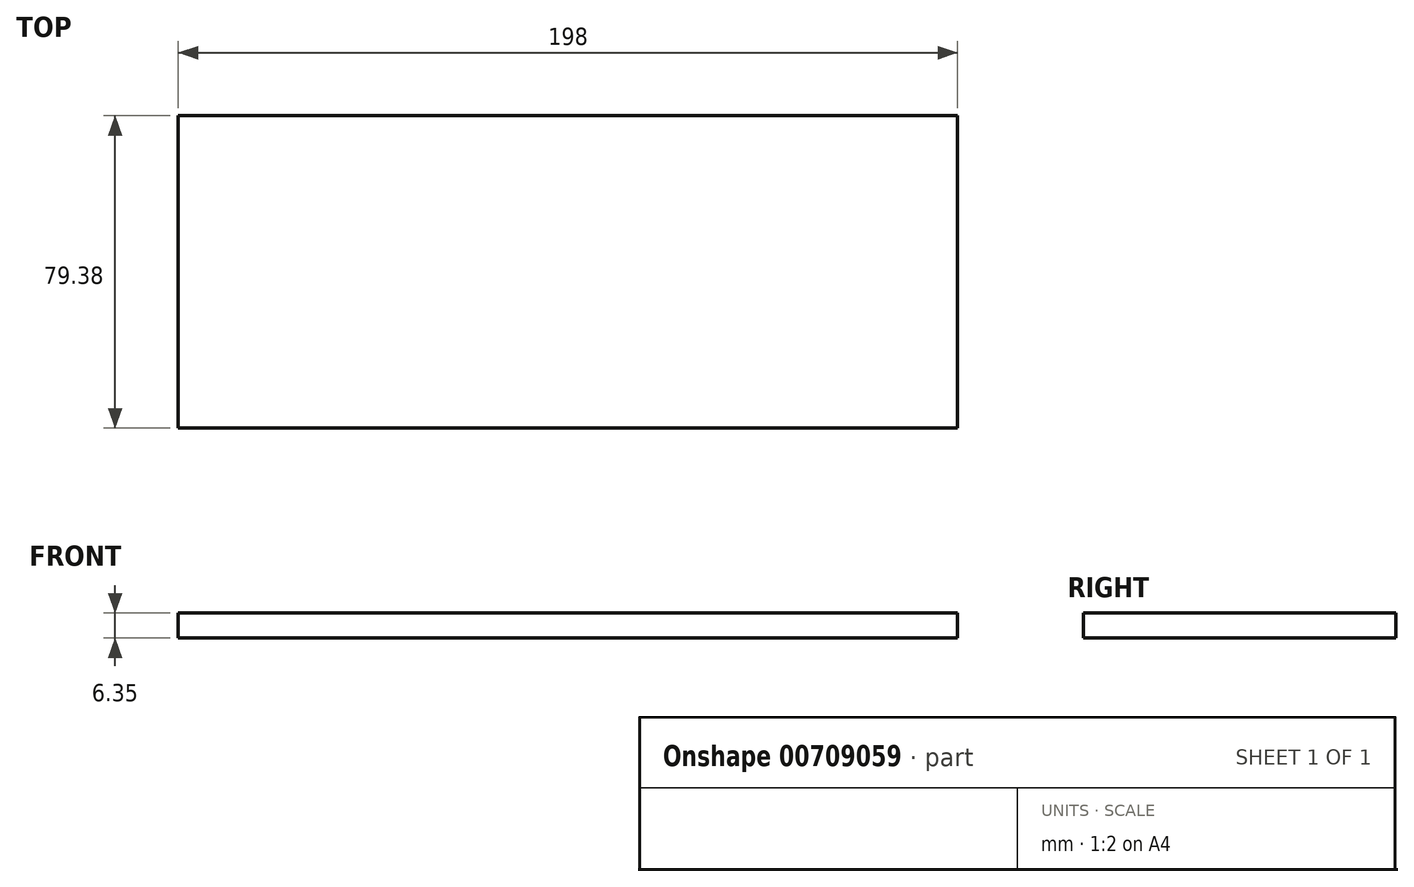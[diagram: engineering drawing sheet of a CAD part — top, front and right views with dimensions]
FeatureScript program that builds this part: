
annotation { "Feature Type Name" : "Feature", "Feature Type Description" : "" }
export const myFeature = defineFeature(function(context is Context, id is Id, definition is map)
    precondition{}
    {
        {
            var Q0;
            Q0=qCreatedBy(makeId("Top.planeOp"),FACE);
            var sketch = newSketch(context, id + "F0", { "sketchPlane" : qUnion([Q0])});
            skLineSegment(sketch, "E0.bottom", {"start": v(0, 0) * mm, "end": v(198, 0) * mm});
            skLineSegment(sketch, "E0.top", {"start": v(0, -79.37) * mm, "end": v(198, -79.37) * mm});
            skLineSegment(sketch, "E0.left", {"start": v(0, 0) * mm, "end": v(0, -79.37) * mm});
            skLineSegment(sketch, "E0.right", {"start": v(198, 0) * mm, "end": v(198, -79.37) * mm});
            skSolve(sketch);
        }
        {
            var Q0;
            Q0=makeQuery(id+"F0.imprint","IMPRINT",FACE,{"disambiguationData":[TD([[makeQuery(id+"F0.imprint","IMPRINT",EDGE,{"derivedFrom":sQuery(id+"F0.wireOp",EDGE,"E0.bottom")}),-1.0]])]});
            extrude(context, id + "F1", {"entities" : qUnion([Q0]), "depth" : 6.35 * mm, "offsetDistance" : 25.4 * mm});
        }
    });
